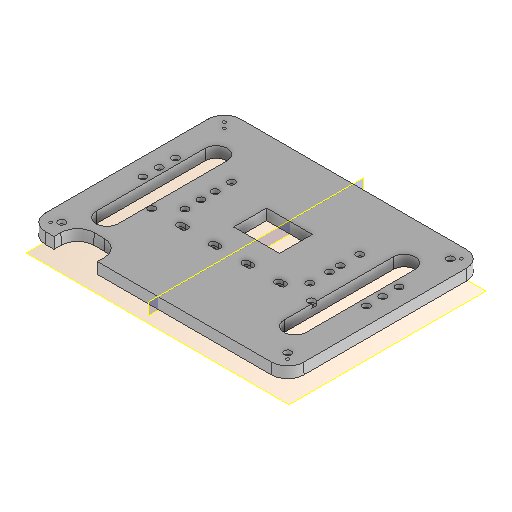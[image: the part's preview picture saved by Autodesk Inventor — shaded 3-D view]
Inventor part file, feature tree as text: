
AUTODESK INVENTOR PART (.ipt)
format: ipt  version: 2024.1 (Build 281209000, 209)  size: 366,592 bytes
history: native  units: mm
features: sketch x6, reference x6, other x5, projected_geometry x4, extrude x3, hole x3, plane x2, mirror x1
ambient origin geometry x8: Origin, YZ Plane, XZ Plane, XY Plane, X Axis, Y Axis, Z Axis, Center Point
bodies: Volumenkörper1 (feature_tree)
feature tree (30):
  plane  "Arbeitsebene1"
  extrude  "Extrusion1"  Depth=3.0mm
  hole  "Bohrung1"  [1 undecoded]
  extrude  "Extrusion3"  TaperAngle=0.0deg  [1 undecoded]
  hole  "Bohrung2"  [1 undecoded]
  plane  "Arbeitsebene2"
  mirror  "Spiegeln1"
  extrude  "Extrusion4"  Depth=3.5mm
  hole  "Bohrung3"  [1 undecoded]
  sketch  "Skizze1"  dims[d0=3.0mm d1=3.0mm]
  reference  "Referenz1"
  reference  "Referenz2"
  reference  "Referenz3"
  sketch  "Skizze3"  dims[d4=15.0mm d5=15.0mm]
  projected_geometry  "Projizierte Kontur2"
  sketch  "Skizze4"  dims[d6=10.0mm d7=-0.174533mm]
  reference  "Referenz4"
  reference  "Referenz5"
  sketch  "Skizze5"  dims[d10=2.8mm d11=6.0mm d12=6.5mm d13=3.5mm d14=90.0deg d15=8.0mm d16=20.594885mm d17=0.0mm d18=0.0mm]
  projected_geometry  "Projizierte Kontur3"
  reference  "Referenz6"
  sketch  "Skizze6"  dims[d19=50.0mm d21=30.0mm d22=10.0mm d24=10.0mm]
  projected_geometry  "Projizierte Kontur4"
  sketch  "Skizze7"  dims[d26=2.8mm d27=6.0mm d28=4.0mm d29=2.0mm d30=90.0deg d31=8.0mm d32=20.594885mm d34=20.0mm d36=15.0mm d37=20.0mm d39=15.0mm d42=1.5mm d43=1.5mm d44=50.0mm d45=20.0mm d46=20.0mm d47=0.0mm d48=0.0mm d49=2.8mm d50=6.0mm d51=6.5mm d52=3.5mm d53=90.0deg d54=8.0mm d55=150.0deg d56=5.0mm]
  projected_geometry  "Projizierte Kontur5"
  other  "Assembly_Planktoscope_Uc2version_wormdrive_V3.iam"
  other  "60_Planktoscope_RaspiScreenHolder_v0:1"
  other  "60_Planktoscope_Base_half_wormdrive_1:1"
  other  "60_Planktoscope_Base_half_wormdrive_1_MIR:1"
  other  "00_NEMA_17:1"
note: 4 required parameter values undecoded (feature->parameter linkage not recoverable at this tier; creation-order binding heuristic only, values carry confidence <= 0.55)
